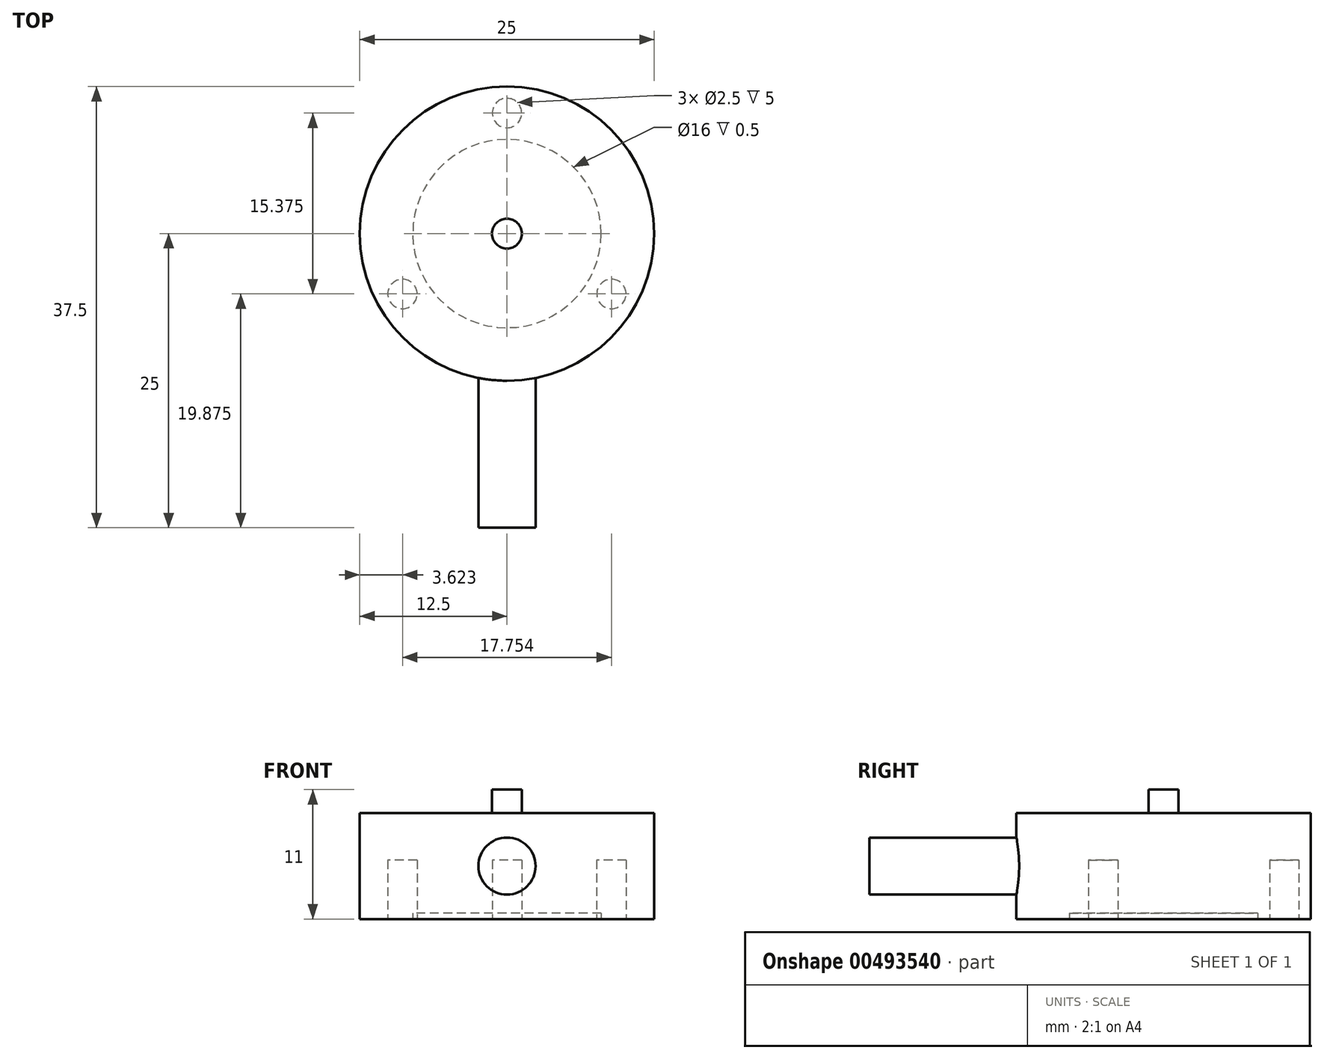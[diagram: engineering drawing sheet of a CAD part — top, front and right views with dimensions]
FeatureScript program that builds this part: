
annotation { "Feature Type Name" : "Feature", "Feature Type Description" : "" }
export const myFeature = defineFeature(function(context is Context, id is Id, definition is map)
    precondition{}
    {
        {
            var Q0;
            Q0=qCreatedBy(makeId("Top.planeOp"),FACE);
            var sketch = newSketch(context, id + "F0", { "sketchPlane" : qUnion([Q0])});
            skCircle(sketch, "E0", {"center": v(0, 0) * mm, "radius": 12.5 * mm});
            skCircle(sketch, "E1", {"center": v(0, 0) * mm, "radius": 8 * mm});
            skCircle(sketch, "E2", {"center": v(0, 10.25) * mm, "radius": 1.25 * mm});
            skCircle(sketch, "E3", {"center": v(-8.88, -5.13) * mm, "radius": 1.25 * mm});
            skCircle(sketch, "E4", {"center": v(8.88, -5.12) * mm, "radius": 1.25 * mm});
            skCircle(sketch, "E5", {"center": v(0, 0) * mm, "radius": 1.27 * mm});
            skLineSegment(sketch, "E6", {"start": v(0, 0) * mm, "end": v(0, 10.25) * mm, "construction": true});
            skLineSegment(sketch, "E7", {"start": v(0, 0) * mm, "end": v(8.88, -5.12) * mm, "construction": true});
            skLineSegment(sketch, "E8", {"start": v(0, 0) * mm, "end": v(-8.88, -5.13) * mm, "construction": true});
            skSolve(sketch);
        }
        {
            var Q0;
            Q0=makeQuery(id+"F0.imprint","IMPRINT",FACE,{"disambiguationData":[TD([[makeQuery(id+"F0.imprint","IMPRINT",EDGE,{"derivedFrom":sQuery(id+"F0.wireOp",EDGE,"E0")}),1.0]])]});
            var Q1;
            Q1=makeQuery(id+"F0.imprint","IMPRINT",FACE,{"disambiguationData":[TD([[makeQuery(id+"F0.imprint","IMPRINT",EDGE,{"derivedFrom":sQuery(id+"F0.wireOp",EDGE,"E1")}),1.0]])]});
            var Q2;
            Q2=makeQuery(id+"F0.imprint","IMPRINT",FACE,{"disambiguationData":[TD([[makeQuery(id+"F0.imprint","IMPRINT",EDGE,{"derivedFrom":sQuery(id+"F0.wireOp",EDGE,"E3")}),1.0]])]});
            var Q3;
            Q3=makeQuery(id+"F0.imprint","IMPRINT",FACE,{"disambiguationData":[TD([[makeQuery(id+"F0.imprint","IMPRINT",EDGE,{"derivedFrom":sQuery(id+"F0.wireOp",EDGE,"E4")}),1.0]])]});
            var Q4;
            Q4=makeQuery(id+"F0.imprint","IMPRINT",FACE,{"disambiguationData":[TD([[makeQuery(id+"F0.imprint","IMPRINT",EDGE,{"derivedFrom":sQuery(id+"F0.wireOp",EDGE,"E5")}),1.0]])]});
            var Q5;
            Q5=makeQuery(id+"F0.imprint","IMPRINT",FACE,{"disambiguationData":[TD([[makeQuery(id+"F0.imprint","IMPRINT",EDGE,{"derivedFrom":sQuery(id+"F0.wireOp",EDGE,"E2")}),1.0]])]});
            extrude(context, id + "F1", {"entities" : qUnion([Q0, Q1, Q2, Q3, Q4, Q5]), "depth" : 9 * mm, "offsetDistance" : 25.4 * mm});
        }
        {
            var Q0;
            Q0=makeQuery(id+"F0.imprint","IMPRINT",FACE,{"disambiguationData":[TD([[makeQuery(id+"F0.imprint","IMPRINT",EDGE,{"derivedFrom":sQuery(id+"F0.wireOp",EDGE,"E5")}),1.0]])]});
            extrude(context, id + "F2", {"entities" : qUnion([Q0]), "operationType" : NewBodyOperationType.ADD, "depth" : 11 * mm, "offsetDistance" : 25.4 * mm});
        }
        {
            var Q0;
            Q0=makeQuery(id+"F0.imprint","IMPRINT",FACE,{"disambiguationData":[TD([[makeQuery(id+"F0.imprint","IMPRINT",EDGE,{"derivedFrom":sQuery(id+"F0.wireOp",EDGE,"E1")}),1.0]])]});
            var Q1;
            Q1=makeQuery(id+"F0.imprint","IMPRINT",FACE,{"disambiguationData":[TD([[makeQuery(id+"F0.imprint","IMPRINT",EDGE,{"derivedFrom":sQuery(id+"F0.wireOp",EDGE,"E5")}),1.0]])]});
            extrude(context, id + "F3", {"entities" : qUnion([Q0, Q1]), "operationType" : NewBodyOperationType.REMOVE, "depth" : .5 * mm, "offsetDistance" : 25.4 * mm});
        }
        {
            var Q0;
            Q0=makeQuery(id+"F0.imprint","IMPRINT",FACE,{"disambiguationData":[TD([[makeQuery(id+"F0.imprint","IMPRINT",EDGE,{"derivedFrom":sQuery(id+"F0.wireOp",EDGE,"E3")}),1.0]])]});
            var Q1;
            Q1=makeQuery(id+"F0.imprint","IMPRINT",FACE,{"disambiguationData":[TD([[makeQuery(id+"F0.imprint","IMPRINT",EDGE,{"derivedFrom":sQuery(id+"F0.wireOp",EDGE,"E4")}),1.0]])]});
            var Q2;
            Q2=makeQuery(id+"F0.imprint","IMPRINT",FACE,{"disambiguationData":[TD([[makeQuery(id+"F0.imprint","IMPRINT",EDGE,{"derivedFrom":sQuery(id+"F0.wireOp",EDGE,"E2")}),1.0]])]});
            extrude(context, id + "F4", {"entities" : qUnion([Q0, Q1, Q2]), "operationType" : NewBodyOperationType.REMOVE, "depth" : 5 * mm, "offsetDistance" : 25.4 * mm});
        }
        {
            var Q0;
            Q0=qCreatedBy(makeId("Front.planeOp"),FACE);
            var sketch = newSketch(context, id + "F5", { "sketchPlane" : qUnion([Q0])});
            skCircle(sketch, "E9", {"center": v(0, 4.5) * mm, "radius": 2.43 * mm});
            skSolve(sketch);
        }
        {
            var Q0;
            Q0 = qSketchRegion(id + "F5", true);
            extrude(context, id + "F6", {"entities" : qUnion([Q0]), "operationType" : NewBodyOperationType.ADD, "depth" : 25 * mm, "offsetDistance" : 25.4 * mm});
        }
    });
